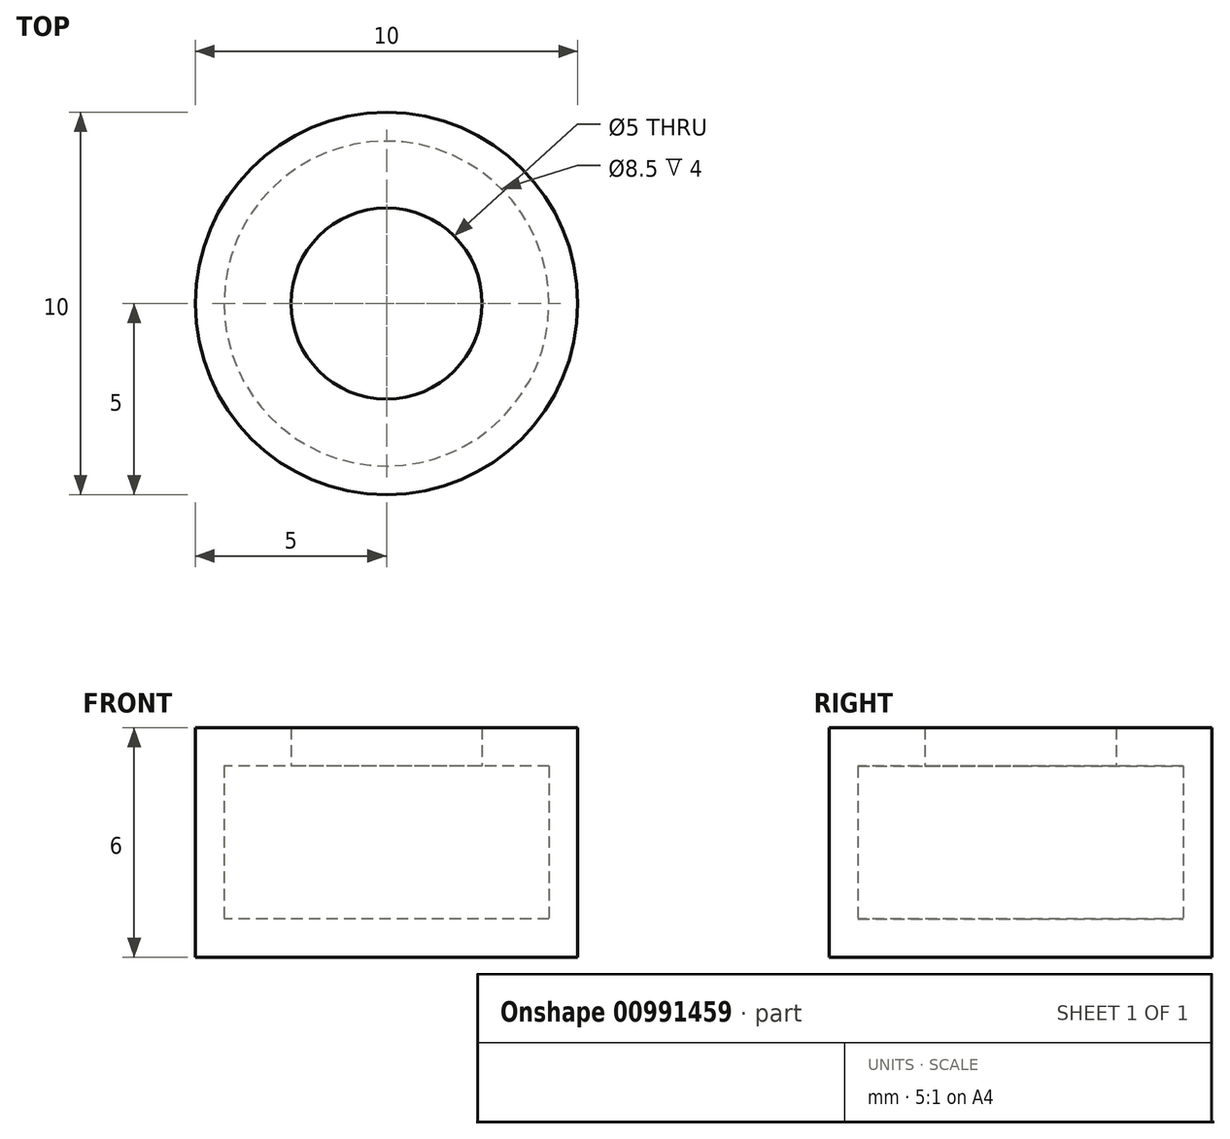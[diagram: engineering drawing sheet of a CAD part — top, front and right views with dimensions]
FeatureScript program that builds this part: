
annotation { "Feature Type Name" : "Feature", "Feature Type Description" : "" }
export const myFeature = defineFeature(function(context is Context, id is Id, definition is map)
    precondition{}
    {
        {
            var Q0;
            Q0=qCreatedBy(makeId("Top.planeOp"),FACE);
            var sketch = newSketch(context, id + "F0", { "sketchPlane" : qUnion([Q0])});
            skCircle(sketch, "E0", {"center": v(0, 0) * mm, "radius": 4.25 * mm});
            skCircle(sketch, "E1", {"center": v(0, 0) * mm, "radius": 5 * mm});
            skCircle(sketch, "E2", {"center": v(0, 0) * mm, "radius": 2.5 * mm});
            skSolve(sketch);
        }
        {
            var Q0;
            Q0=makeQuery(id+"F0.imprint","IMPRINT",FACE,{"disambiguationData":[TD([[makeQuery(id+"F0.imprint","IMPRINT",EDGE,{"derivedFrom":sQuery(id+"F0.wireOp",EDGE,"E0")}),1.0]])]});
            var Q1;
            Q1=makeQuery(id+"F0.imprint","IMPRINT",FACE,{"disambiguationData":[TD([[makeQuery(id+"F0.imprint","IMPRINT",EDGE,{"derivedFrom":sQuery(id+"F0.wireOp",EDGE,"E0")}),-1.0]])]});
            var Q2;
            Q2=makeQuery(id+"F0.imprint","IMPRINT",FACE,{"disambiguationData":[TD([[makeQuery(id+"F0.imprint","IMPRINT",EDGE,{"derivedFrom":sQuery(id+"F0.wireOp",EDGE,"E2")}),1.0]])]});
            extrude(context, id + "F1", {"entities" : qUnion([Q0, Q1, Q2]), "depth" : 1 * mm, "offsetDistance" : 25 * mm});
        }
        {
            var Q0;
            Q0=makeQuery(id+"F0.imprint","IMPRINT",FACE,{"disambiguationData":[TD([[makeQuery(id+"F0.imprint","IMPRINT",EDGE,{"derivedFrom":sQuery(id+"F0.wireOp",EDGE,"E0")}),-1.0]])]});
            extrude(context, id + "F2", {"entities" : qUnion([Q0]), "operationType" : NewBodyOperationType.ADD, "depth" : 6 * mm, "offsetDistance" : 25 * mm});
        }
        {
            var Q0;
            Q0=makeQuery(id+"F0.imprint","IMPRINT",FACE,{"disambiguationData":[TD([[makeQuery(id+"F0.imprint","IMPRINT",EDGE,{"derivedFrom":sQuery(id+"F0.wireOp",EDGE,"E0")}),1.0]])]});
            extrude(context, id + "F3", {"entities" : qUnion([Q0]), "operationType" : NewBodyOperationType.ADD, "depth" : 6 * mm, "offsetDistance" : 25 * mm, "hasSecondDirection" : true, "secondDirectionOppositeDirection" : true, "secondDirectionDepth" : -5 * mm});
        }
    });
